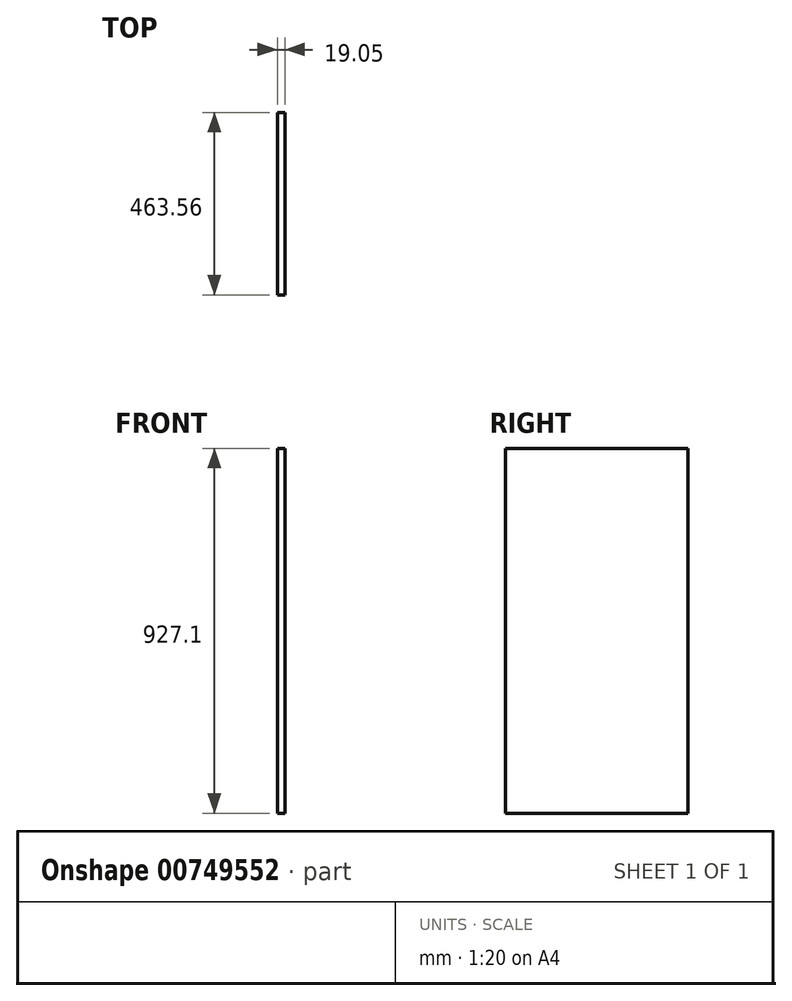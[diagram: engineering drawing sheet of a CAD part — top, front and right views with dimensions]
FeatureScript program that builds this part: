
annotation { "Feature Type Name" : "Feature", "Feature Type Description" : "" }
export const myFeature = defineFeature(function(context is Context, id is Id, definition is map)
    precondition{}
    {
        {
            var Q0;
            Q0=qCreatedBy(makeId("Right.planeOp"),FACE);
            var sketch = newSketch(context, id + "F0", { "sketchPlane" : qUnion([Q0])});
            skLineSegment(sketch, "E0.bottom", {"start": v(231.77, 463.55) * mm, "end": v(-231.78, 463.55) * mm});
            skLineSegment(sketch, "E0.top", {"start": v(231.77, -463.55) * mm, "end": v(-231.78, -463.55) * mm});
            skLineSegment(sketch, "E0.left", {"start": v(231.77, 463.55) * mm, "end": v(231.77, -463.55) * mm});
            skLineSegment(sketch, "E0.right", {"start": v(-231.78, 463.55) * mm, "end": v(-231.78, -463.55) * mm});
            skPoint(sketch, "E0.middle", {"position": v(0, 0) * mm});
            skSolve(sketch);
        }
        {
            var Q0;
            Q0=makeQuery(id+"F0.imprint","IMPRINT",FACE,{"disambiguationData":[TD([[makeQuery(id+"F0.imprint","IMPRINT",EDGE,{"derivedFrom":sQuery(id+"F0.wireOp",EDGE,"E0.bottom")}),1.0]])]});
            extrude(context, id + "F1", {"entities" : qUnion([Q0]), "depth" : 19.05 * mm, "offsetDistance" : 25.4 * mm});
        }
    });
